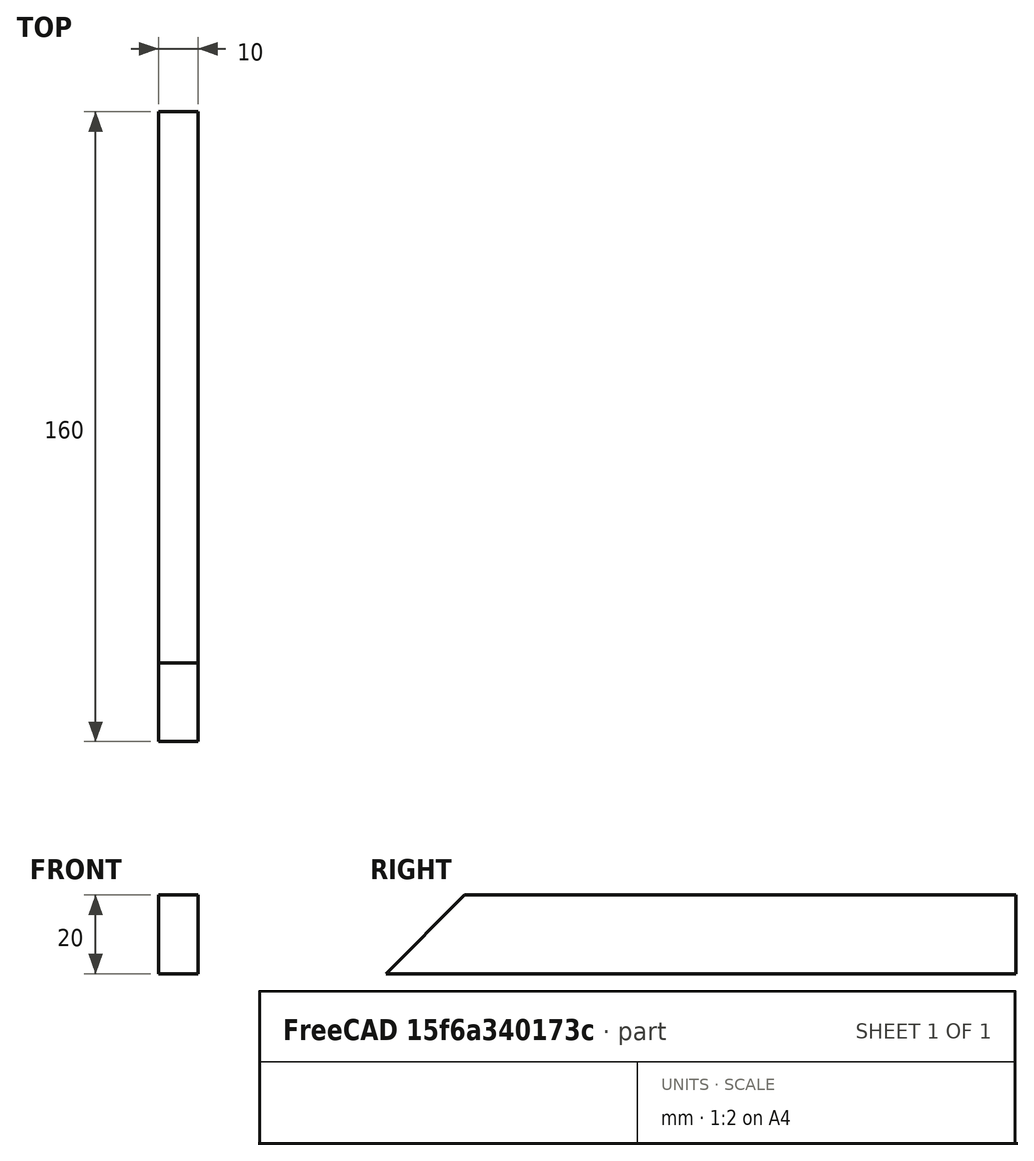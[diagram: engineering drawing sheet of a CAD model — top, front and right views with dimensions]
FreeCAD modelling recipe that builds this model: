
FCSTD DOCUMENT  (FreeCAD 0.18R4 (GitTag))
Label: Divider-C
License: All rights reserved
LicenseURL: http://en.wikipedia.org/wiki/All_rights_reserved
objects: Sketcher::SketchObject×1, PartDesign::Pad×1, PartDesign::Body×1
note: 4 computed .brp shape members not serialized (recipe doc carries the construction recipe); baked Part::Feature solids carry a one-line shape summary decoded from their .brp

FEATURE [Sketcher::SketchObject] Sketch
  MapMode = 5
  Placement = pos=(0,0,0) rot=(0.57735,0.57735,0.57735;2.0944rad)
  Support = -> [YZ_Plane]
  sketch-geometry (4):
    g0: LineSegment StartX=0 StartY=0 StartZ=0 EndX=-160 EndY=0 EndZ=0
    g1: LineSegment StartX=-160 StartY=0 StartZ=0 EndX=-140 EndY=20 EndZ=0
    g2: LineSegment StartX=-140 StartY=20 StartZ=0 EndX=0 EndY=20 EndZ=0
    g3: LineSegment StartX=0 StartY=20 StartZ=0 EndX=0 EndY=0 EndZ=0
  constraints (10):
    c: Coincident(g0,g1)
    c: Coincident(g1,g2)
    c: Coincident(g2,g3)
    c: Coincident(g3,g0)
    c: Tangent(g3,g-2)
    c: Horizontal(g2)
    c: Tangent(g0,g-1)
    c: Distance(g3) = 20
    c: Distance(g0) = 160
    c: Distance(g2) = 140
FEATURE [PartDesign::Pad] Pad
  Length = 10
  Length2 = 100
  Placement = pos=(0,0,0) rot=(0.57735,0.57735,0.57735;2.0944rad)
  Profile = -> Sketch
  Type = 0
FEATURE [PartDesign::Body] Body
  Group = -> [Sketch,Pad]
  Origin = -> Origin
  Tip = -> Pad
